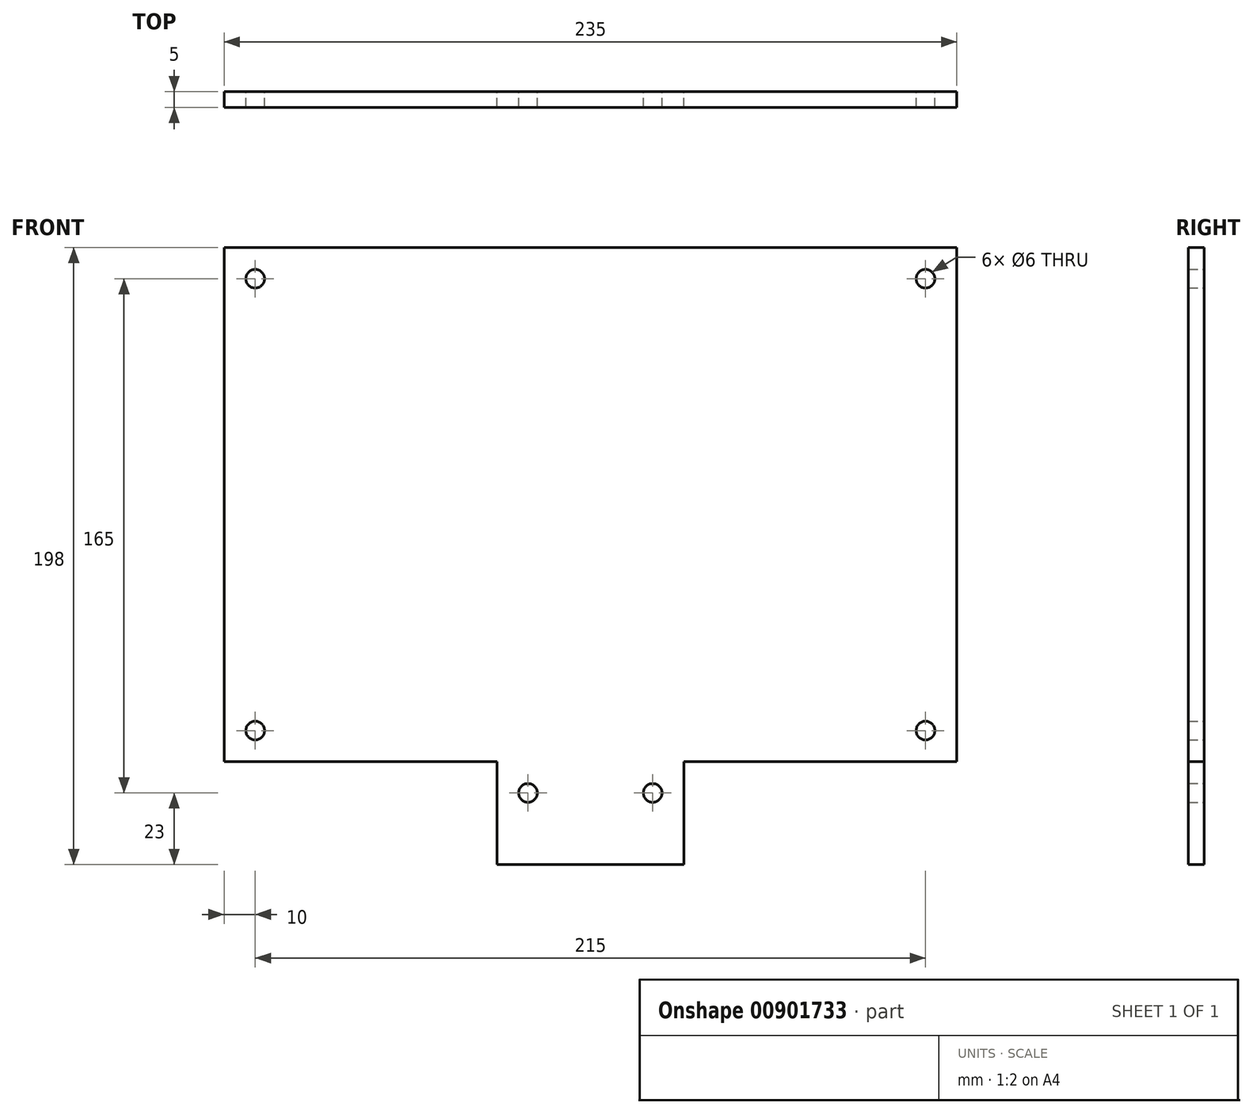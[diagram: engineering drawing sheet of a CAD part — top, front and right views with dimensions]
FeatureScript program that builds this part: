
annotation { "Feature Type Name" : "Feature", "Feature Type Description" : "" }
export const myFeature = defineFeature(function(context is Context, id is Id, definition is map)
    precondition{}
    {
        {
            var Q0;
            Q0=qCreatedBy(makeId("Front.planeOp"),FACE);
            var sketch = newSketch(context, id + "F0", { "sketchPlane" : qUnion([Q0])});
            skLineSegment(sketch, "E0", {"start": v(0, 0) * mm, "end": v(0, 33) * mm});
            skLineSegment(sketch, "E1", {"start": v(0, 33) * mm, "end": v(-87.5, 33) * mm});
            skLineSegment(sketch, "E2", {"start": v(-87.5, 33) * mm, "end": v(-87.5, 198) * mm});
            skLineSegment(sketch, "E3", {"start": v(-87.5, 198) * mm, "end": v(147.5, 198) * mm});
            skLineSegment(sketch, "E4", {"start": v(147.5, 198) * mm, "end": v(147.5, 33) * mm});
            skLineSegment(sketch, "E5", {"start": v(147.5, 33) * mm, "end": v(60, 33) * mm});
            skLineSegment(sketch, "E6", {"start": v(60, 33) * mm, "end": v(60, 0) * mm});
            skLineSegment(sketch, "E7", {"start": v(60, 0) * mm, "end": v(0, 0) * mm});
            skCircle(sketch, "E8", {"center": v(-77.5, 188) * mm, "radius": 3 * mm});
            skCircle(sketch, "E9", {"center": v(137.5, 188) * mm, "radius": 3 * mm});
            skCircle(sketch, "E10", {"center": v(137.5, 43) * mm, "radius": 3 * mm});
            skCircle(sketch, "E11", {"center": v(-77.5, 43) * mm, "radius": 3 * mm});
            skCircle(sketch, "E12", {"center": v(10, 23) * mm, "radius": 3 * mm});
            skCircle(sketch, "E13", {"center": v(50, 23) * mm, "radius": 3 * mm});
            skSolve(sketch);
        }
        {
            var Q0;
            Q0=makeQuery(id+"F0.imprint","IMPRINT",FACE,{"disambiguationData":[TD([[makeQuery(id+"F0.imprint","IMPRINT",EDGE,{"derivedFrom":sQuery(id+"F0.wireOp",EDGE,"E0")}),-1.0]])]});
            extrude(context, id + "F1", {"entities" : qUnion([Q0]), "depth" : 5 * mm, "offsetDistance" : 25 * mm});
        }
    });
